AUTODESK INVENTOR PART (.ipt)
format: ipt  version: 2015 (Build 190159000, 159)  size: 128,512 bytes
history: native  units: mm
features: sketch x7, projected_geometry x5, extrude x4, plane x1
ambient origin geometry x8: Origin, YZ Plane, XZ Plane, XY Plane, X Axis, Y Axis, Z Axis, Center Point
bodies: Solid1 (feature_tree)
feature tree (17):
  sketch  "Sketch1"  dims[d0=310.0mm d1=310.0mm]
  extrude  "Extrusion1"  Depth=310.0mm
  extrude  "Extrusion2"  Depth=280.0mm TaperAngle=0.0deg
  sketch  "Sketch4"  dims[d2=10.0mm d3=0.0mm d4=280.0mm d5=0.0mm]
  sketch  "Sketch5"  dims[d6=310.0mm d7=310.0mm]
  sketch  "Sketch6"  dims[d8=270.0mm d9=270.0mm d10=0.0mm]
  sketch  "Sketch7"  dims[d11=270.0mm d12=0.0mm]
  extrude  "Extrusion3"  Depth=310.0mm
  extrude  "Extrusion4"  Depth=270.0mm TaperAngle=0.0deg
  plane  "Work Plane1"
  projected_geometry  "Projected Loop1"
  projected_geometry  "Projected Loop2"
  projected_geometry  "Projected Loop3"
  projected_geometry  "Projected Loop4"
  sketch  "Sketch8"  dims[d13=10.0mm]
  sketch  "Sketch9"
  projected_geometry  "Projected Loop5"
